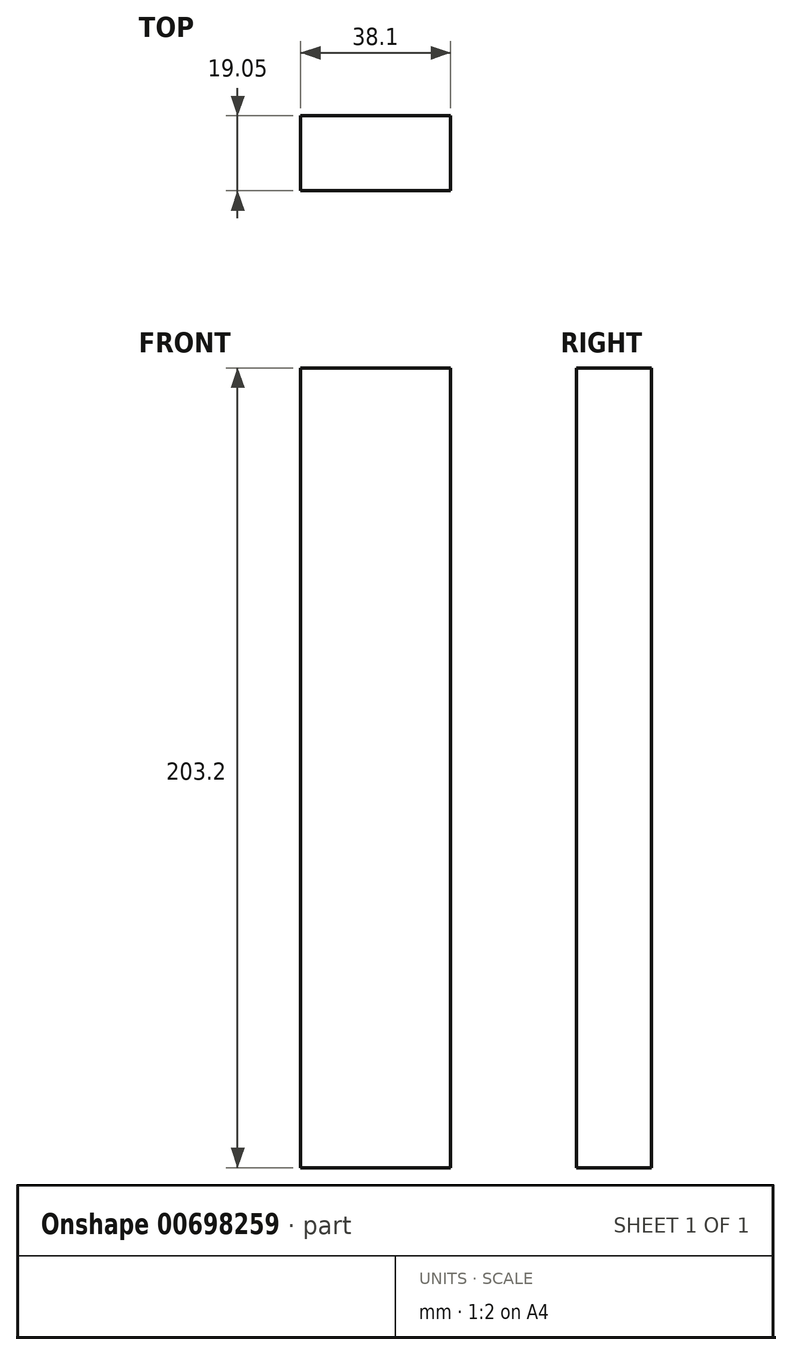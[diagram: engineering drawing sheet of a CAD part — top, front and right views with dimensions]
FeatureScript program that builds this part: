
annotation { "Feature Type Name" : "Feature", "Feature Type Description" : "" }
export const myFeature = defineFeature(function(context is Context, id is Id, definition is map)
    precondition{}
    {
        {
            var Q0;
            Q0=qCreatedBy(makeId("Front.planeOp"),FACE);
            var sketch = newSketch(context, id + "F0", { "sketchPlane" : qUnion([Q0])});
            skLineSegment(sketch, "E0.bottom", {"start": v(-37.73, 133.75) * mm, "end": v(0.37, 133.75) * mm});
            skLineSegment(sketch, "E0.top", {"start": v(-37.73, -69.45) * mm, "end": v(0.37, -69.45) * mm});
            skLineSegment(sketch, "E0.left", {"start": v(-37.73, 133.75) * mm, "end": v(-37.73, -69.45) * mm});
            skLineSegment(sketch, "E0.right", {"start": v(0.37, 133.75) * mm, "end": v(0.37, -69.45) * mm});
            skSolve(sketch);
        }
        {
            var Q0;
            Q0=makeQuery(id+"F0.imprint","IMPRINT",FACE,{"disambiguationData":[TD([[makeQuery(id+"F0.imprint","IMPRINT",EDGE,{"derivedFrom":sQuery(id+"F0.wireOp",EDGE,"E0.bottom")}),-1.0]])]});
            extrude(context, id + "F1", {"entities" : qUnion([Q0]), "depth" : 19.05 * mm, "offsetDistance" : 25.4 * mm});
        }
    });
